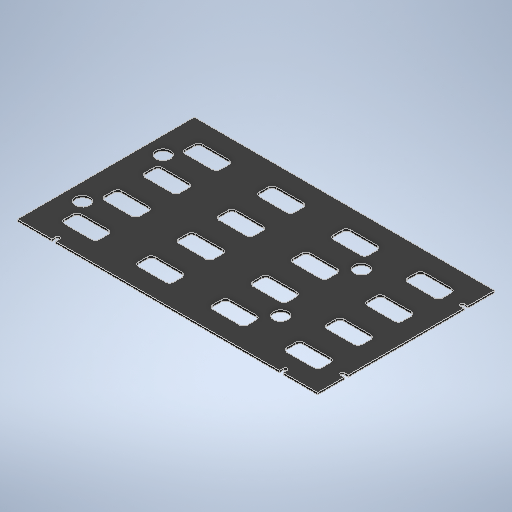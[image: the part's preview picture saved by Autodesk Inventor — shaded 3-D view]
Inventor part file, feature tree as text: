
AUTODESK INVENTOR PART (.ipt)
format: ipt  version: 2025 (Build 290162000, 162)  size: 474,112 bytes
history: native  units: mm
features: extrude x2, sketch x2
ambient origin geometry x8: Origin, YZ Plane, XZ Plane, XY Plane, X Axis, Y Axis, Z Axis, Center Point
bodies: Solid1 (feature_tree)
feature tree (4):
  extrude  "Extrusion1"  Depth=3.000318mm
  extrude  "Extrusion2"  Depth=3.0mm
  sketch  "Sketch1"  dims[d0=1.5875mm d1=0.0mm d2=3.000318mm]
  sketch  "Sketch2"  dims[d3=3.0mm d4=3.0mm d5=3.0mm d6=0.0mm d7=0.0mm]
